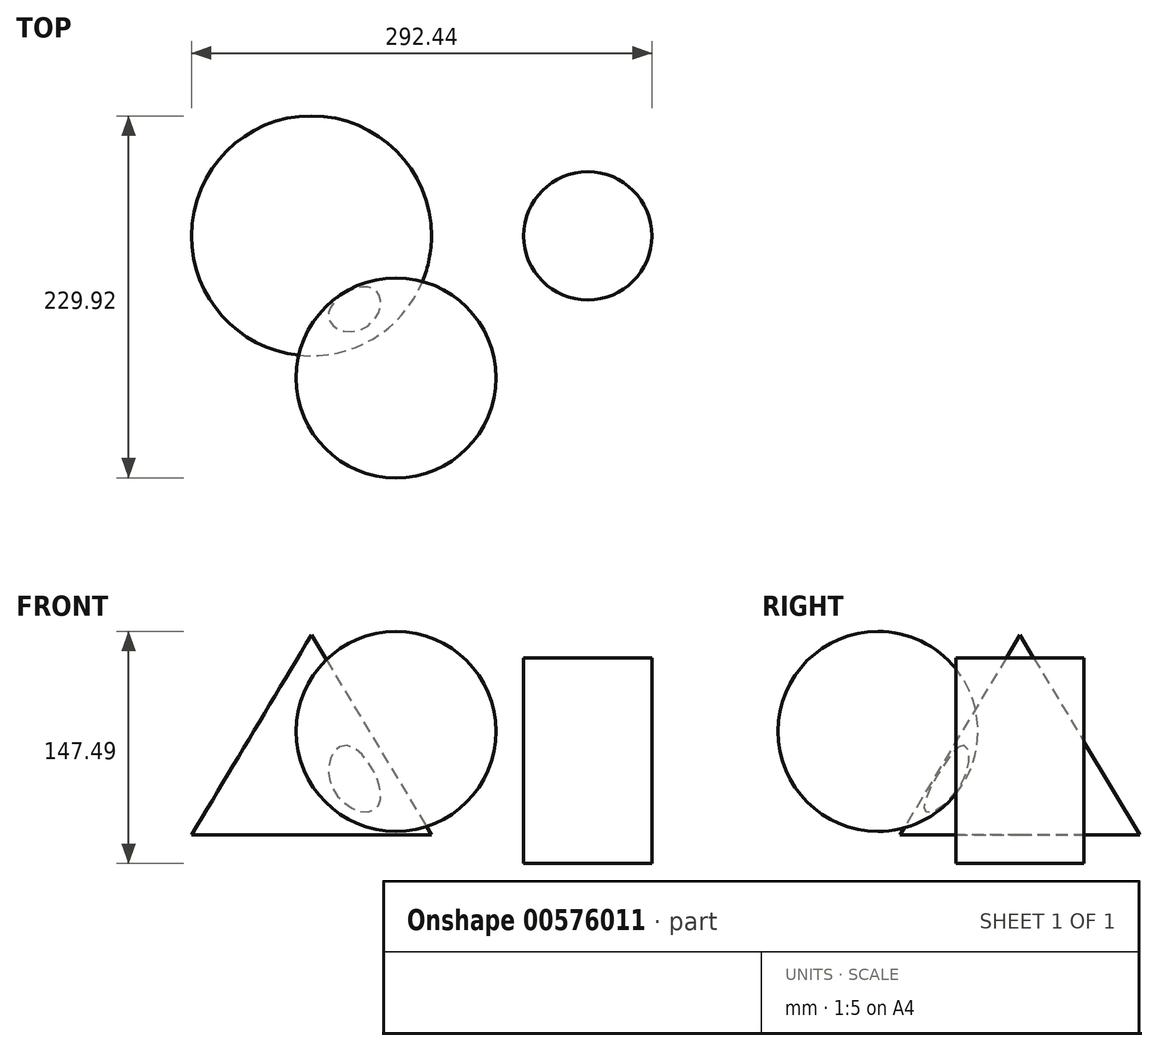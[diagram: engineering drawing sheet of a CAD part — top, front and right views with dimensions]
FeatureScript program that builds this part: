
annotation { "Feature Type Name" : "Feature", "Feature Type Description" : "" }
export const myFeature = defineFeature(function(context is Context, id is Id, definition is map)
    precondition{}
    {
        {
            var Q0;
            Q0=qCreatedBy(makeId("Front.planeOp"),FACE);
            var sketch = newSketch(context, id + "F0", { "sketchPlane" : qUnion([Q0])});
            skLineSegment(sketch, "E0", {"start": v(-53.7, 61.37) * mm, "end": v(-53.7, -65.63) * mm});
            skLineSegment(sketch, "E1", {"start": v(-53.7, -65.63) * mm, "end": v(-129.9, -65.63) * mm});
            skLineSegment(sketch, "E2", {"start": v(-129.9, -65.63) * mm, "end": v(-53.7, 61.37) * mm});
            skSolve(sketch);
        }
        {
            var Q0;
            Q0=makeQuery(id+"F0.imprint","IMPRINT",FACE,{"disambiguationData":[TD([[makeQuery(id+"F0.imprint","IMPRINT",EDGE,{"derivedFrom":sQuery(id+"F0.wireOp",EDGE,"E0")}),-1.0]])]});
            var Q1;
            Q1=sQuery(id+"F0.wireOp",EDGE,"E0");
            revolve(context, id + "F1", {"entities" : qUnion([Q0]), "axis" : qUnion([Q1]), "revolveType" : RevolveType.ONE_DIRECTION, "angle" : 360 * degree});
        }
        {
            var Q0;
            Q0=qCreatedBy(makeId("Right.planeOp"),FACE);
            var sketch = newSketch(context, id + "F2", { "sketchPlane" : qUnion([Q0])});
            skLineSegment(sketch, "E3", {"start": v(-90.22, 63.65) * mm, "end": v(-90.22, -63.35) * mm});
            skCircle(sketch, "E4", {"center": v(-90.22, 0.15) * mm, "radius": 63.5 * mm});
            skSolve(sketch);
        }
        {
            var Q0;
            {var subQ0=sQuery(id+"F2.wireOp",EDGE,"E3");Q0=makeQuery(id+"F2.imprint","IMPRINT",FACE,{"disambiguationData":[TD([[makeQuery(id+"F2.imprint","IMPRINT",EDGE,{"derivedFrom":subQ0}),1.0]])]});}
            var Q1;
            Q1=sQuery(id+"F2.wireOp",EDGE,"E3");
            revolve(context, id + "F3", {"operationType" : NewBodyOperationType.ADD, "entities" : qUnion([Q0]), "axis" : qUnion([Q1]), "revolveType" : RevolveType.FULL});
        }
        {
            var Q0;
            Q0=qCreatedBy(makeId("Front.planeOp"),FACE);
            var sketch = newSketch(context, id + "F4", { "sketchPlane" : qUnion([Q0])});
            skLineSegment(sketch, "E5", {"start": v(121.8, 46.87) * mm, "end": v(121.8, -83.84) * mm});
            skLineSegment(sketch, "E6", {"start": v(121.8, -83.84) * mm, "end": v(162.55, -83.84) * mm});
            skLineSegment(sketch, "E7", {"start": v(162.55, -83.84) * mm, "end": v(162.55, 46.87) * mm});
            skLineSegment(sketch, "E8", {"start": v(162.55, 46.87) * mm, "end": v(121.8, 46.87) * mm});
            skSolve(sketch);
        }
        {
            var Q0;
            Q0 = qSketchRegion(id + "F4", true);
            var Q1;
            Q1=sQuery(id+"F4.wireOp",EDGE,"E5");
            revolve(context, id + "F5", {"entities" : qUnion([Q0]), "axis" : qUnion([Q1]), "revolveType" : RevolveType.FULL});
        }
    });
